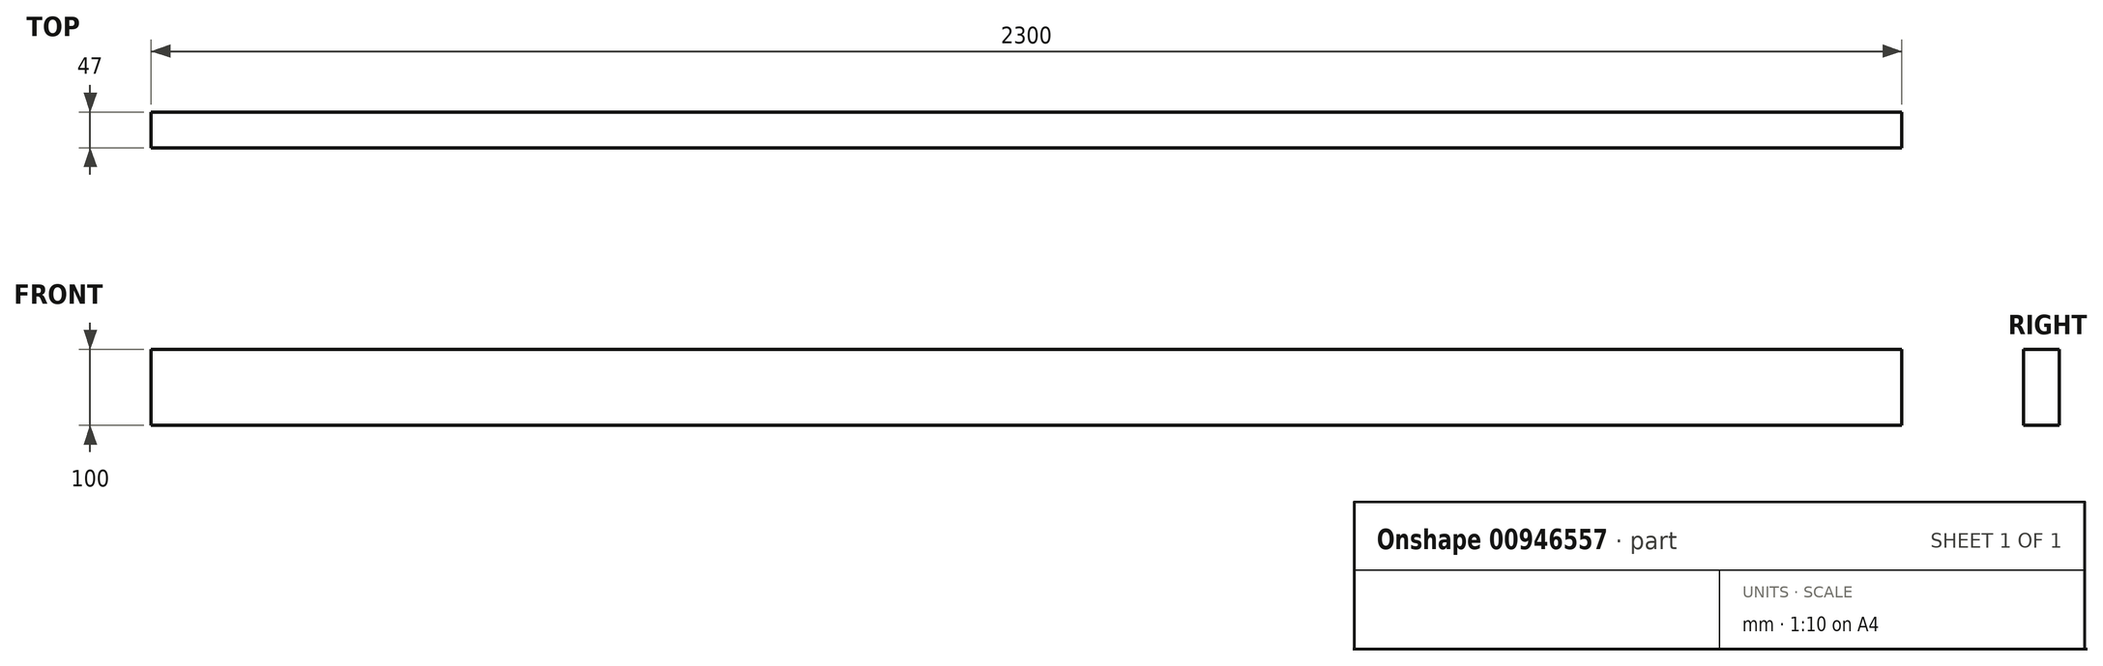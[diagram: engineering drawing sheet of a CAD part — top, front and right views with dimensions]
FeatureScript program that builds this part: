
annotation { "Feature Type Name" : "Feature", "Feature Type Description" : "" }
export const myFeature = defineFeature(function(context is Context, id is Id, definition is map)
    precondition{}
    {
        {
            var Q0;
            Q0=qCreatedBy(makeId("Right.planeOp"),FACE);
            var sketch = newSketch(context, id + "F0", { "sketchPlane" : qUnion([Q0])});
            skLineSegment(sketch, "E0.bottom", {"start": v(0, 0) * mm, "end": v(-47, 0) * mm});
            skLineSegment(sketch, "E0.top", {"start": v(0, 100) * mm, "end": v(-47, 100) * mm});
            skLineSegment(sketch, "E0.left", {"start": v(0, 0) * mm, "end": v(0, 100) * mm});
            skLineSegment(sketch, "E0.right", {"start": v(-47, 0) * mm, "end": v(-47, 100) * mm});
            skSolve(sketch);
        }
        {
            var Q0;
            Q0=qSketchRegion(id+"F0",true);
            extrude(context, id + "F1", {"entities" : qUnion([Q0]), "depth" : 2300 * mm, "offsetDistance" : 25 * mm});
        }
    });
